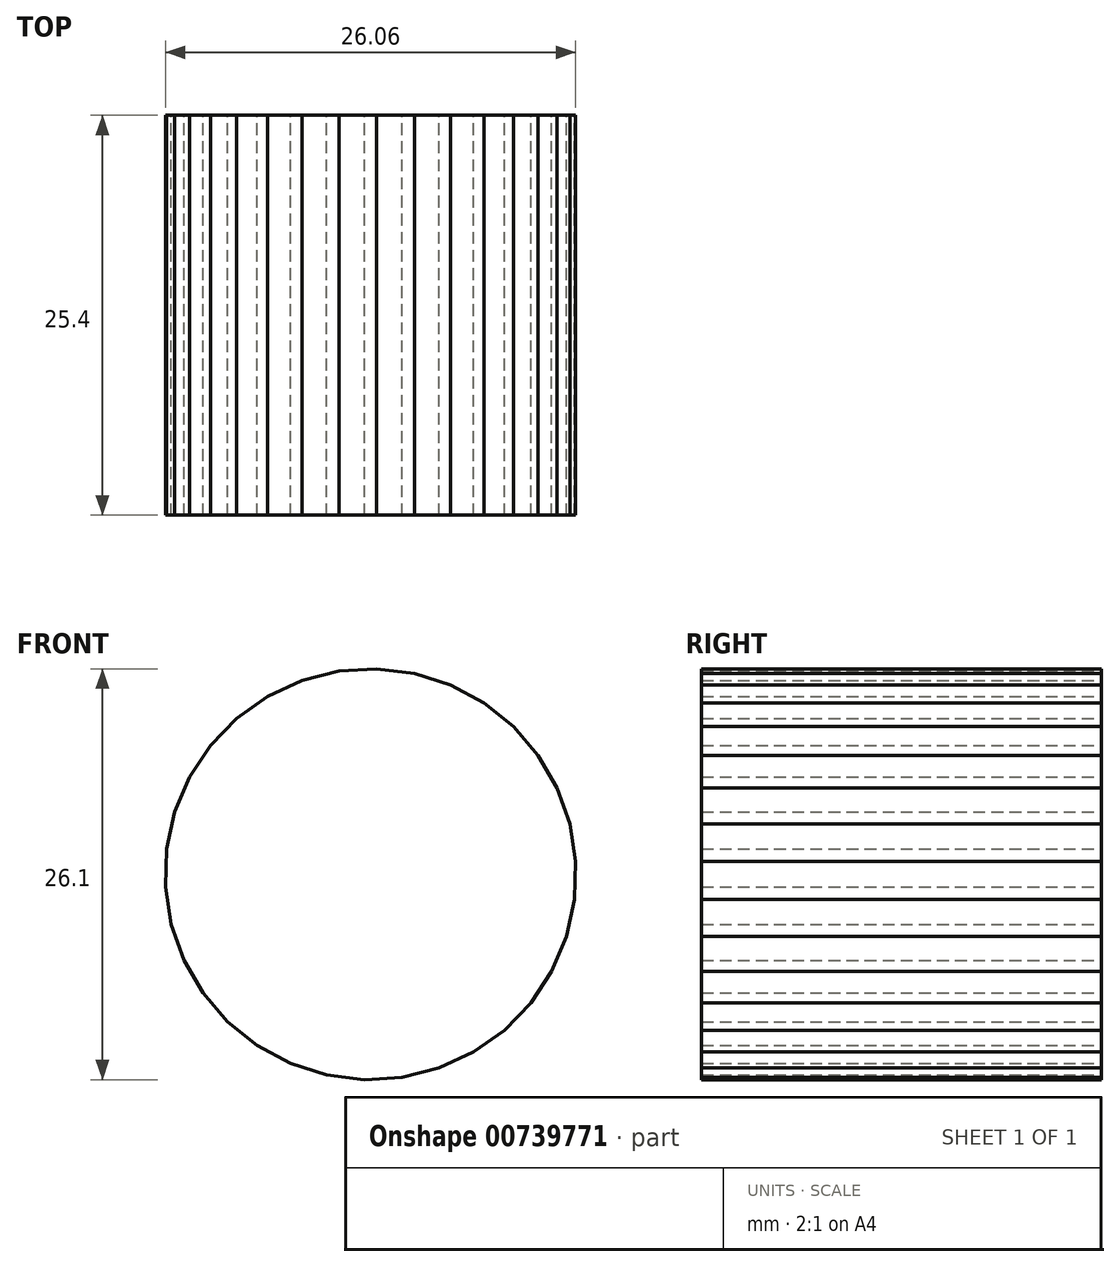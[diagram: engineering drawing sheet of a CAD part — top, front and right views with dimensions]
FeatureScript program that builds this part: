
annotation { "Feature Type Name" : "Feature", "Feature Type Description" : "" }
export const myFeature = defineFeature(function(context is Context, id is Id, definition is map)
    precondition{}
    {
        {
            var Q0;
            Q0=qCreatedBy(makeId("Front.planeOp"),FACE);
            var sketch = newSketch(context, id + "F0", { "sketchPlane" : qUnion([Q0])});
            skCircle(sketch, "E0.cCircle", {"center": v(0, 0) * mm, "radius": 13 * mm, "construction": true});
            skLineSegment(sketch, "E0.0", {"start": v(12.96, -1.6) * mm, "end": v(12.44, -3.95) * mm});
            skLineSegment(sketch, "E0.1", {"start": v(12.44, -3.95) * mm, "end": v(11.5, -6.16) * mm});
            skLineSegment(sketch, "E0.2", {"start": v(11.5, -6.16) * mm, "end": v(10.18, -8.17) * mm});
            skLineSegment(sketch, "E0.3", {"start": v(10.18, -8.17) * mm, "end": v(8.5, -9.9) * mm});
            skLineSegment(sketch, "E0.4", {"start": v(8.5, -9.9) * mm, "end": v(6.54, -11.3) * mm});
            skLineSegment(sketch, "E0.5", {"start": v(6.54, -11.3) * mm, "end": v(4.35, -12.3) * mm});
            skLineSegment(sketch, "E0.6", {"start": v(4.35, -12.3) * mm, "end": v(2.01, -12.9) * mm});
            skLineSegment(sketch, "E0.7", {"start": v(2.01, -12.9) * mm, "end": v(-0.4, -13.05) * mm});
            skLineSegment(sketch, "E0.8", {"start": v(-0.4, -13.05) * mm, "end": v(-2.78, -12.75) * mm});
            skLineSegment(sketch, "E0.9", {"start": v(-2.78, -12.75) * mm, "end": v(-5.08, -12.02) * mm});
            skLineSegment(sketch, "E0.10", {"start": v(-5.08, -12.02) * mm, "end": v(-7.2, -10.89) * mm});
            skLineSegment(sketch, "E0.11", {"start": v(-7.2, -10.89) * mm, "end": v(-9.08, -9.38) * mm});
            skLineSegment(sketch, "E0.12", {"start": v(-9.08, -9.38) * mm, "end": v(-10.65, -7.55) * mm});
            skLineSegment(sketch, "E0.13", {"start": v(-10.65, -7.55) * mm, "end": v(-11.85, -5.47) * mm});
            skLineSegment(sketch, "E0.14", {"start": v(-11.85, -5.47) * mm, "end": v(-12.66, -3.2) * mm});
            skLineSegment(sketch, "E0.15", {"start": v(-12.66, -3.2) * mm, "end": v(-13.03, -0.82) * mm});
            skLineSegment(sketch, "E0.16", {"start": v(-13.03, -0.82) * mm, "end": v(-12.96, 1.6) * mm});
            skLineSegment(sketch, "E0.17", {"start": v(-12.96, 1.6) * mm, "end": v(-12.44, 3.95) * mm});
            skLineSegment(sketch, "E0.18", {"start": v(-12.44, 3.95) * mm, "end": v(-11.5, 6.16) * mm});
            skLineSegment(sketch, "E0.19", {"start": v(-11.5, 6.16) * mm, "end": v(-10.18, 8.17) * mm});
            skLineSegment(sketch, "E0.20", {"start": v(-10.18, 8.17) * mm, "end": v(-8.5, 9.9) * mm});
            skLineSegment(sketch, "E0.21", {"start": v(-8.5, 9.9) * mm, "end": v(-6.54, 11.3) * mm});
            skLineSegment(sketch, "E0.22", {"start": v(-6.54, 11.3) * mm, "end": v(-4.35, 12.3) * mm});
            skLineSegment(sketch, "E0.23", {"start": v(-4.35, 12.3) * mm, "end": v(-2.01, 12.9) * mm});
            skLineSegment(sketch, "E0.24", {"start": v(-2.01, 12.9) * mm, "end": v(0.4, 13.05) * mm});
            skLineSegment(sketch, "E0.25", {"start": v(0.4, 13.05) * mm, "end": v(2.78, 12.75) * mm});
            skLineSegment(sketch, "E0.26", {"start": v(2.78, 12.75) * mm, "end": v(5.08, 12.02) * mm});
            skLineSegment(sketch, "E0.27", {"start": v(5.08, 12.02) * mm, "end": v(7.2, 10.89) * mm});
            skLineSegment(sketch, "E0.28", {"start": v(7.2, 10.89) * mm, "end": v(9.08, 9.38) * mm});
            skLineSegment(sketch, "E0.29", {"start": v(9.08, 9.38) * mm, "end": v(10.65, 7.55) * mm});
            skLineSegment(sketch, "E0.30", {"start": v(10.65, 7.55) * mm, "end": v(11.85, 5.47) * mm});
            skLineSegment(sketch, "E0.31", {"start": v(11.85, 5.47) * mm, "end": v(12.66, 3.2) * mm});
            skLineSegment(sketch, "E0.32", {"start": v(12.66, 3.2) * mm, "end": v(13.03, 0.82) * mm});
            skLineSegment(sketch, "E0.33", {"start": v(13.03, 0.82) * mm, "end": v(12.96, -1.6) * mm});
            skPoint(sketch, "E0.0.midPoint", {"position": v(12.7, -2.77) * mm});
            skSolve(sketch);
        }
        {
            var Q0;
            Q0 = qSketchRegion(id + "F0", true);
            extrude(context, id + "F1", {"entities" : qUnion([Q0]), "depth" : 25.4 * mm, "offsetDistance" : 25.4 * mm});
        }
    });
